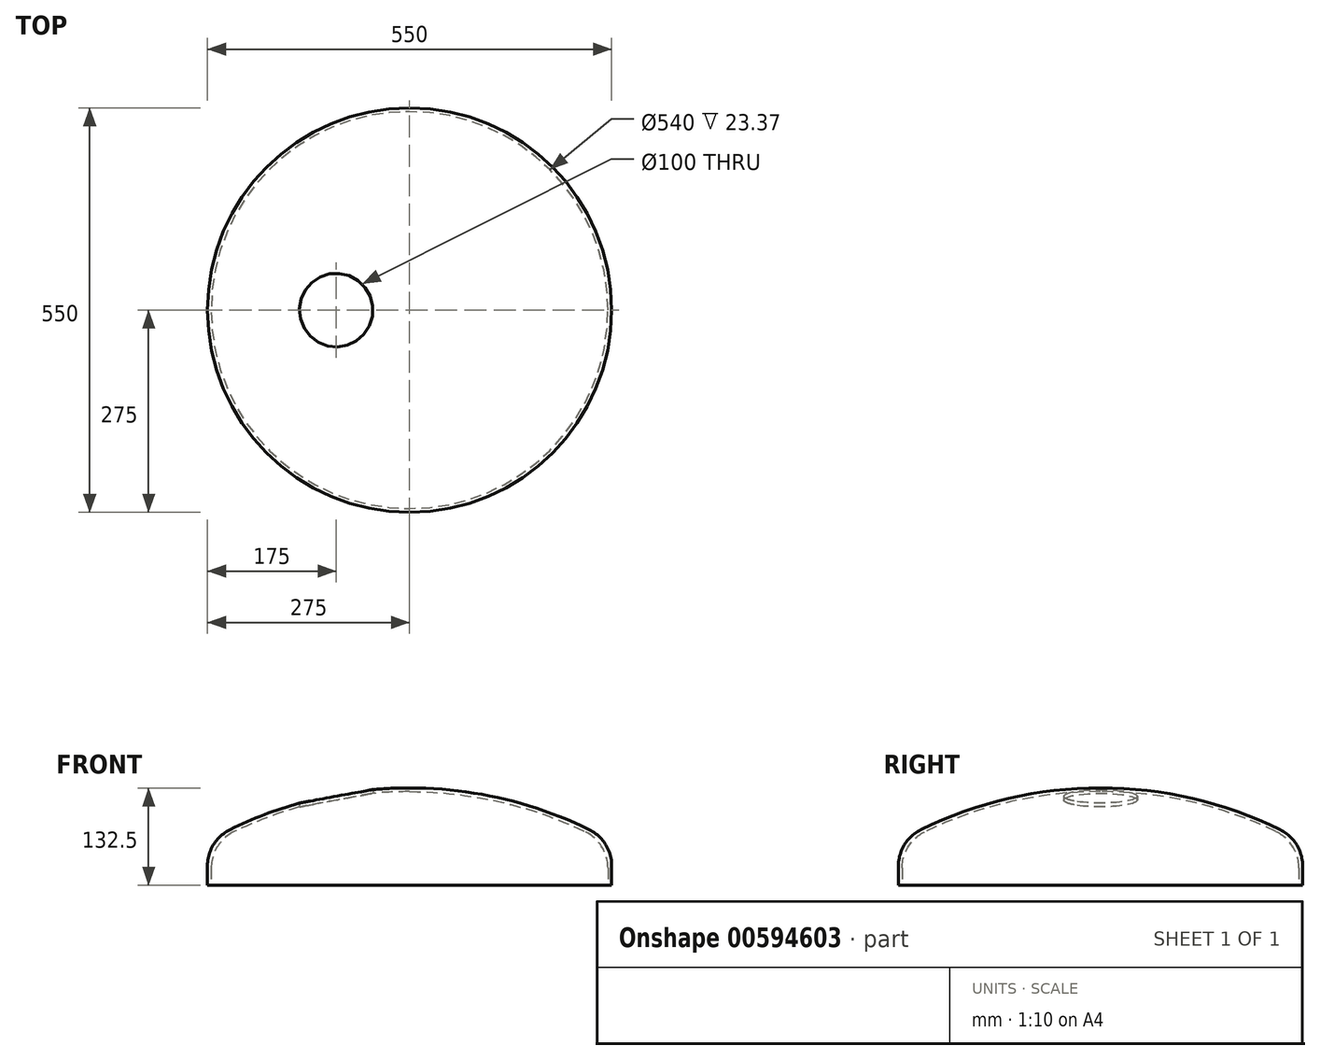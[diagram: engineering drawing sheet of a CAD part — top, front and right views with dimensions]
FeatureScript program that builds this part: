
annotation { "Feature Type Name" : "Feature", "Feature Type Description" : "" }
export const myFeature = defineFeature(function(context is Context, id is Id, definition is map)
    precondition{}
    {
        {
            var Q0;
            Q0=qCreatedBy(makeId("Front.planeOp"),FACE);
            var sketch = newSketch(context, id + "F0", { "sketchPlane" : qUnion([Q0])});
            skArc(sketch, "E0", {"start": v(-275, 476.31) * mm, "mid": v(0, -550) * mm, "end": v(275, 476.31) * mm});
            skLineSegment(sketch, "E1", {"start": v(0, 0) * mm, "end": v(721.01, 0) * mm});
            skLineSegment(sketch, "E2", {"start": v(275, 482.08) * mm, "end": v(275, 0) * mm});
            skCircle(sketch, "E3", {"center": v(0, 0) * mm, "radius": 555 * mm});
            skLineSegment(sketch, "E4", {"start": v(270, 479.17) * mm, "end": v(270, 0) * mm});
            skLineSegment(sketch, "E5", {"start": v(0, 0) * mm, "end": v(0, 190.02) * mm});
            skLineSegment(sketch, "E6.MirrorCS", {"start": v(540, 0) * mm, "end": v(540, 190.02) * mm});
            skLineSegment(sketch, "E7.MirrorCS", {"start": v(-270, 479.17) * mm, "end": v(-270, 0) * mm});
            skLineSegment(sketch, "E8.MirrorCS", {"start": v(-275, 482.08) * mm, "end": v(-275, 0) * mm});
            skLineSegment(sketch, "E9", {"start": v(270, 422.5) * mm, "end": v(275, 422.5) * mm});
            skArc(sketch, "E10.trimOffspring", {"start": v(270, 479.17) * mm, "mid": v(0, 550) * mm, "end": v(-270, 479.17) * mm});
            skLineSegment(sketch, "E11.trimOffspring", {"start": v(-275, 422.5) * mm, "end": v(-270, 422.5) * mm});
            skLineSegment(sketch, "E12", {"start": v(0, 0) * mm, "end": v(0, 678.68) * mm});
            skSolve(sketch);
        }
        {
            var Q0;
            {var subQ3=sQuery(id+"F0.wireOp",EDGE,"E9");Q0=makeQuery(id+"F0.imprint","IMPRINT",FACE,{"disambiguationData":[TD([[makeQuery(id+"F0.imprint","IMPRINT",EDGE,{"derivedFrom":subQ3}),1.0]])]});}
            var Q1;
            Q1=sQuery(id+"F0.wireOp",EDGE,"E12");
            revolve(context, id + "F1", {"entities" : qUnion([Q0]), "axis" : qUnion([Q1]), "revolveType" : RevolveType.FULL});
        }
        {
            var Q0;
            Q0=makeQuery(id+"F1.opRevolve","SWEPT_EDGE",EDGE,{"disambiguationData":[OSD([sQuery(id+"F0.wireOp",EDGE,"E4"),sQuery(id+"F0.wireOp",EDGE,"E10.trimOffspring")])]});
            fillet(context, id + "F2", {"entities" : qUnion([Q0]), "radius" : (0.1 * 550) * mm, "tangentPropagation" : true, "allowEdgeOverflow" : false});
        }
        {
            var Q0;
            Q0=makeQuery(id+"F1.opRevolve","SWEPT_EDGE",EDGE,{"disambiguationData":[OSD([sQuery(id+"F0.wireOp",EDGE,"E2"),sQuery(id+"F0.wireOp",EDGE,"E3")])]});
            fillet(context, id + "F3", {"entities" : qUnion([Q0]), "radius" : (0.1 * 550) * mm, "tangentPropagation" : true, "allowEdgeOverflow" : false});
        }
        {
            var Q0;
            Q0=makeQuery(id+"F1.opRevolve","SWEPT_FACE",FACE,{"disambiguationData":[OSD([sQuery(id+"F0.wireOp",EDGE,"E9")])]});
            var sketch = newSketch(context, id + "F4", { "sketchPlane" : qUnion([Q0])});
            skCircle(sketch, "E13", {"center": v(-100, 0) * mm, "radius": 50 * mm});
            skSolve(sketch);
        }
        {
            var Q0;
            Q0=makeQuery(id+"F4.imprint","IMPRINT",FACE,{"disambiguationData":[TD([[makeQuery(id+"F4.imprint","IMPRINT",EDGE,{"derivedFrom":sQuery(id+"F4.wireOp",EDGE,"E13")}),1.0]])]});
            extrude(context, id + "F5", {"entities" : qUnion([Q0]), "operationType" : NewBodyOperationType.REMOVE, "endBound" : BoundingType.THROUGH_ALL, "oppositeDirection" : true, "depth" : 25 * mm, "offsetDistance" : 25 * mm});
        }
    });
